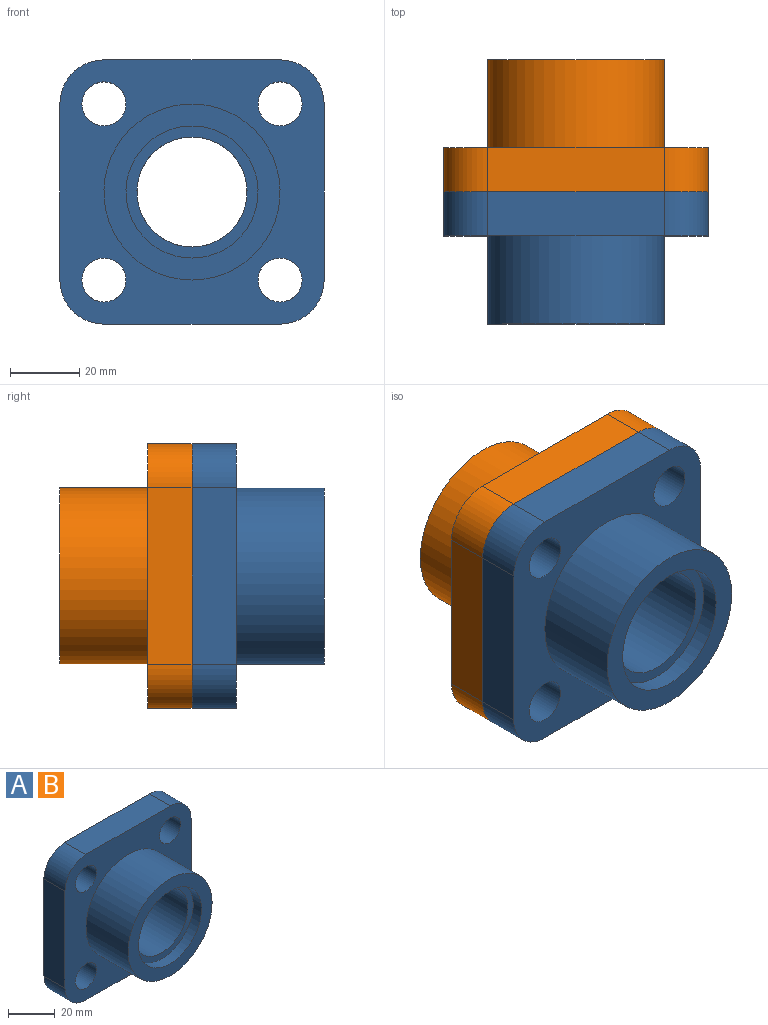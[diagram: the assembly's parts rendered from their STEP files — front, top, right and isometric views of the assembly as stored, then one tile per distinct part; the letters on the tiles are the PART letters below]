
ASSEMBLY  parts=2 mates=1
PART A: 19 faces, bbox 76.2x38.1x76.2 mm
  f0: plane 50.8x12.7mm, normal (1,0,0), area 645.2mm2, adj f1,f11,f12,f13
  f1: cylinder r=12.7mm len=12.7mm, axis (0,1,0), area 253.4mm2, adj f0,f2,f12,f13
  f2: plane 50.8x12.7mm, normal (0,0,1), area 645.2mm2, adj f1,f3,f12,f13
  f3: cylinder r=12.7mm len=12.7mm, axis (0,1,0), area 253.4mm2, adj f2,f4,f12,f13
  f4: plane 50.8x12.7mm, normal (-1,0,0), area 645.2mm2, adj f3,f5,f12,f13
  f5: cylinder r=12.7mm len=12.7mm, axis (0,1,0), area 253.4mm2, adj f4,f6,f12,f13
  f6: plane 50.8x12.7mm, normal (0,0,-1), area 645.2mm2, adj f5,f11,f12,f13
  f7: cylinder r=6.35mm len=12.7mm, axis (0,1,0), area 506.7mm2, adj f12,f13
  f8: cylinder r=6.35mm len=12.7mm, axis (0,1,0), area 506.7mm2, adj f12,f13
  f9: cylinder r=6.35mm len=12.7mm, axis (0,1,0), area 506.7mm2, adj f12,f13
  f10: cylinder r=6.35mm len=12.7mm, axis (0,1,0), area 506.7mm2, adj f12,f13
  f11: cylinder r=12.7mm len=12.7mm, axis (0,1,0), area 253.4mm2, adj f0,f6,f12,f13
  f12: plane 76.2x76.2mm, normal (0,-1,0), area 3134.5mm2, adj f0,f1,f2,f3,f4,f5,f6,f7
  f13: plane 76.2x76.2mm, normal (0,1,0), area 4369.5mm2, adj f0,f1,f2,f3,f4,f5,f6,f7
  f14: cylinder r=25.4mm len=50.8mm, axis (0,1,0), area 4053.7mm2, adj f12,f15
  f15: plane 50.8x50.8mm, normal (0,-1,0), area 886.7mm2, adj f14,f16
  f16: cylinder r=19.05mm len=38.1mm, axis (0,-1,0), area 608mm2, adj f15,f17
  f17: plane 38.1x38.1mm, normal (0,-1,0), area 348.4mm2, adj f16,f18
  f18: cylinder r=15.88mm len=33.02mm, axis (0,-1,0), area 3293.6mm2, adj f13,f17
PART B: same geometry as A
PLACE A t=(-10.52,13.27,0.44)mm
PLACE B rot(axis=(1,0,0),180deg) t=(-10.52,13.27,0.44)mm
MATE planar B.f13 <-> A.f13  axis (0,-1,0) through (27.58,13.27,0.44)mm
